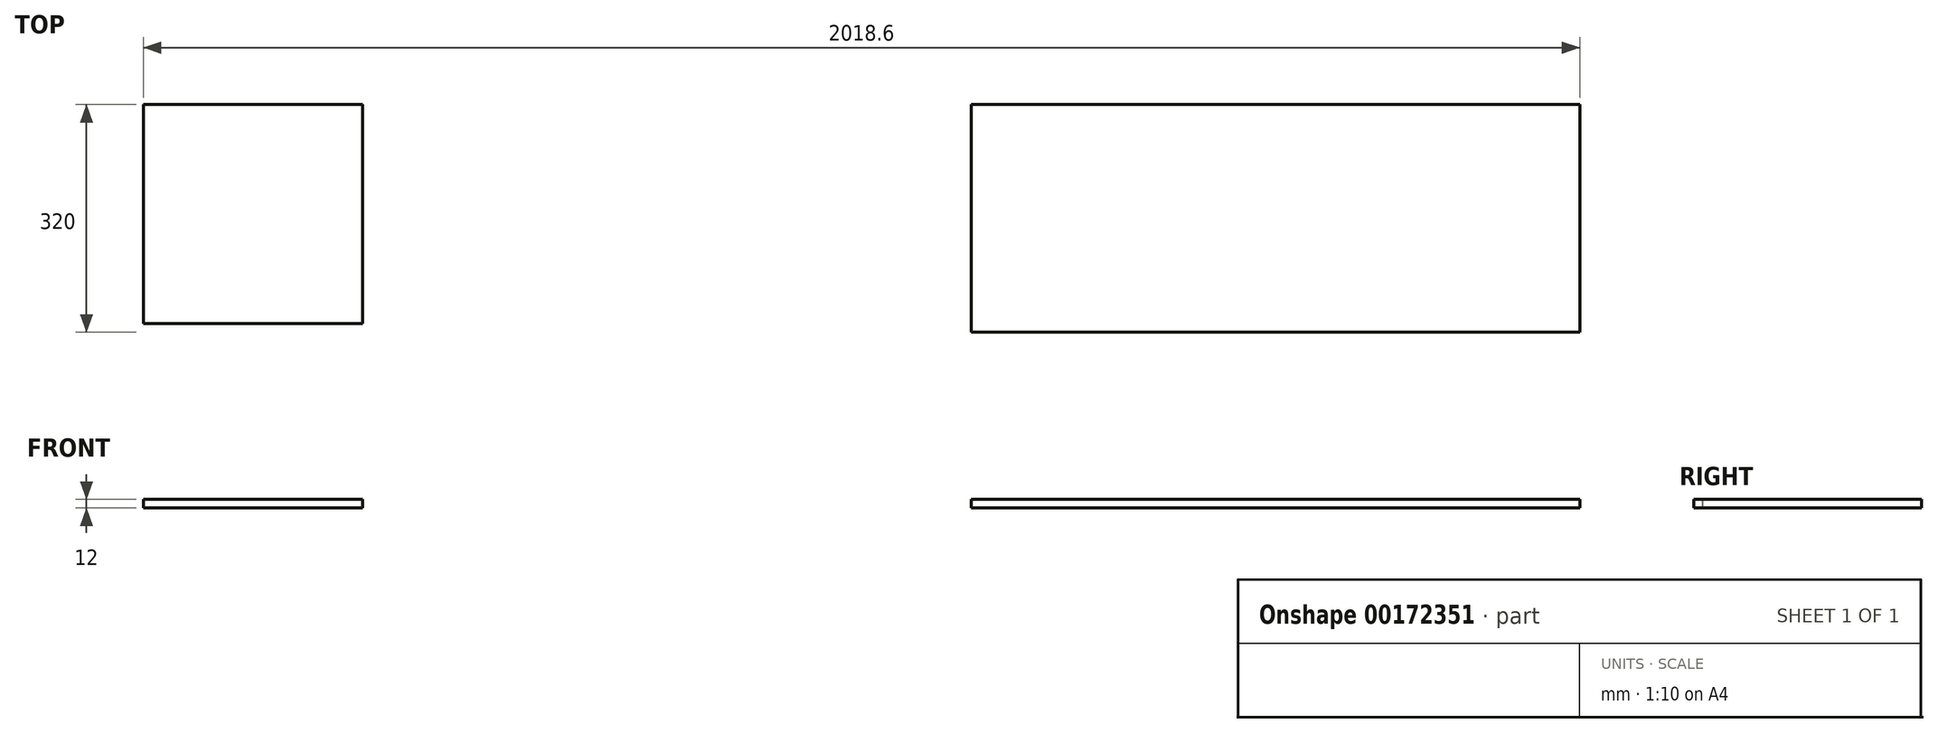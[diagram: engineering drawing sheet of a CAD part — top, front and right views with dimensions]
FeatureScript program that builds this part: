
annotation { "Feature Type Name" : "Feature", "Feature Type Description" : "" }
export const myFeature = defineFeature(function(context is Context, id is Id, definition is map)
    precondition{}
    {
        {
            var Q0;
            Q0=qCreatedBy(makeId("Top.planeOp"),FACE);
            var sketch = newSketch(context, id + "F0", { "sketchPlane" : qUnion([Q0])});
            skLineSegment(sketch, "E0.bottom", {"start": v(-1400, 1035) * mm, "end": v(1400, 1035) * mm});
            skLineSegment(sketch, "E0.top", {"start": v(-1400, -1035) * mm, "end": v(1400, -1035) * mm});
            skLineSegment(sketch, "E0.left", {"start": v(-1400, 1035) * mm, "end": v(-1400, -1035) * mm});
            skLineSegment(sketch, "E0.right", {"start": v(1400, 1035) * mm, "end": v(1400, -1035) * mm});
            skPoint(sketch, "E0.middle", {"position": v(0, 0) * mm});
            skLineSegment(sketch, "E1.bottom", {"start": v(-1400, 1035) * mm, "end": v(-1079.8, 1035) * mm});
            skLineSegment(sketch, "E1.top", {"start": v(-1400, 714.8) * mm, "end": v(-1079.8, 714.8) * mm});
            skLineSegment(sketch, "E1.left", {"start": v(-1400, 1035) * mm, "end": v(-1400, 714.8) * mm});
            skLineSegment(sketch, "E1.right", {"start": v(-1079.8, 1035) * mm, "end": v(-1079.8, 714.8) * mm});
            skLineSegment(sketch, "E2.bottom", {"start": v(-1079.8, 714.8) * mm, "end": v(-759.4, 714.8) * mm});
            skLineSegment(sketch, "E2.top", {"start": v(-1079.8, 1035) * mm, "end": v(-759.4, 1035) * mm});
            skLineSegment(sketch, "E2.left", {"start": v(-1079.8, 714.8) * mm, "end": v(-1079.8, 1035) * mm});
            skLineSegment(sketch, "E2.right", {"start": v(-759.4, 714.8) * mm, "end": v(-759.4, 1035) * mm});
            skLineSegment(sketch, "E3.bottom", {"start": v(-759.4, 1035) * mm, "end": v(-451.2, 1035) * mm});
            skLineSegment(sketch, "E3.top", {"start": v(-759.4, 727) * mm, "end": v(-451.2, 727) * mm});
            skLineSegment(sketch, "E3.left", {"start": v(-759.4, 1035) * mm, "end": v(-759.4, 727) * mm});
            skLineSegment(sketch, "E3.right", {"start": v(-451.2, 1035) * mm, "end": v(-451.2, 727) * mm});
            skLineSegment(sketch, "E4.bottom", {"start": v(-451.2, 1035) * mm, "end": v(404, 1035) * mm});
            skLineSegment(sketch, "E4.top", {"start": v(-451.2, 715) * mm, "end": v(404, 715) * mm});
            skLineSegment(sketch, "E4.left", {"start": v(-451.2, 1035) * mm, "end": v(-451.2, 715) * mm});
            skLineSegment(sketch, "E4.right", {"start": v(404, 1035) * mm, "end": v(404, 715) * mm});
            skLineSegment(sketch, "E5.bottom", {"start": v(404, 1035) * mm, "end": v(1259.2, 1035) * mm});
            skLineSegment(sketch, "E5.top", {"start": v(404, 715) * mm, "end": v(1259.2, 715) * mm});
            skLineSegment(sketch, "E5.right", {"start": v(1259.2, 1035) * mm, "end": v(1259.2, 715) * mm});
            skLineSegment(sketch, "E6.bottom", {"start": v(-1400, 714.8) * mm, "end": v(-1091.8, 714.8) * mm});
            skLineSegment(sketch, "E6.top", {"start": v(-1400, 406.6) * mm, "end": v(-1091.8, 406.6) * mm});
            skLineSegment(sketch, "E6.left", {"start": v(-1400, 714.8) * mm, "end": v(-1400, 406.6) * mm});
            skLineSegment(sketch, "E6.right", {"start": v(-1091.8, 714.8) * mm, "end": v(-1091.8, 406.6) * mm});
            skSolve(sketch);
        }
        {
            var Q0;
            Q0=makeQuery(id+"F0.imprint","IMPRINT",FACE,{"disambiguationData":[TD([[makeQuery(id+"F0.imprint","IMPRINT",EDGE,{"derivedFrom":sQuery(id+"F0.wireOp",EDGE,"E0.bottom")}),-1.0]])]});
            extrude(context, id + "F1", {"entities" : qUnion([Q0]), "depth" : 12 * mm});
        }
    });
